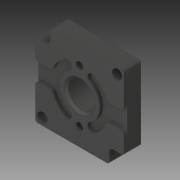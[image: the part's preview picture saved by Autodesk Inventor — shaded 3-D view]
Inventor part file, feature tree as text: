
AUTODESK INVENTOR PART (.ipt)
format: ipt  version: 2019 (Build 230136000, 136)  size: 286,208 bytes
history: native  units: in
note: dims shown in document units (in); Inventor stores cm internally (conversion verified against a paired STEP export)
features: fillet x1
ambient origin geometry x8: Origin, YZ Plane, XZ Plane, XY Plane, X Axis, Y Axis, Z Axis, Center Point
bodies: Solid1 (feature_tree)
feature tree (1):
  fillet  "Fillet4"  [1 undecoded]
note: 1 required parameter value undecoded (feature->parameter linkage not recoverable at this tier; creation-order binding heuristic only, values carry confidence <= 0.55)
